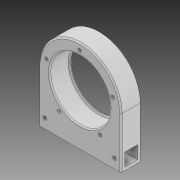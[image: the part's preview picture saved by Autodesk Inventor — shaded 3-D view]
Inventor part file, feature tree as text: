
AUTODESK INVENTOR PART (.ipt)
format: ipt  version: 2020 (Build 240168000, 168)  size: 304,128 bytes
history: native  units: mm
features: extrude x6, sketch x6, chamfer x2, plane x1, fillet x1
ambient origin geometry x8: Origin, YZ Plane, XZ Plane, XY Plane, X Axis, Y Axis, Z Axis, Center Point
bodies: Solid1 (feature_tree)
feature tree (16):
  extrude  "Extrusion1"  Depth=80.0mm
  extrude  "Extrusion2"  Depth=2.0mm
  extrude  "Extrusion3"  Depth=1.0mm
  plane  "Work Plane1"
  fillet  "Fillet1"  Radius=55.0mm
  chamfer  "Chamfer1"  Distance=50.0mm Angle=360.0deg
  chamfer  "Chamfer2"  [1 undecoded]
  extrude  "Extrusion8"  Depth=2.0mm
  extrude  "Extrusion9"  Depth=2.0mm TaperAngle=45.0deg
  extrude  "Extrusion10"  Depth=20.5mm
  sketch  "Sketch1"  dims[d0=95.05mm d2=80.0mm]
  sketch  "Sketch2"  dims[d3=32.5mm d4=0.0mm d5=2.0mm]
  sketch  "Sketch3"  dims[d6=1.0mm d7=0.0mm d8=5.2mm d9=55.0mm d10=50.0mm d12=360.0deg d14=0.0mm d15=0.0mm]
  sketch  "Sketch9"  dims[d22=-15.0mm d28=2.0mm]
  sketch  "Sketch10"  dims[d29=2.0mm d30=2.0mm d31=45.0deg d40=2.0mm d41=2.0mm d42=45.0deg]
  sketch  "Sketch11"  dims[d43=65.0mm d48=20.5mm d49=20.5mm d50=15.0mm d51=0.0mm d52=0.0mm d53=5.5mm d54=10.0mm d55=10.0mm d56=0.0mm d57=0.0mm d58=8.3mm d59=50.0mm d61=360.0deg d63=15.25mm d64=0.0mm]
note: 1 required parameter value undecoded (feature->parameter linkage not recoverable at this tier; creation-order binding heuristic only, values carry confidence <= 0.55)
